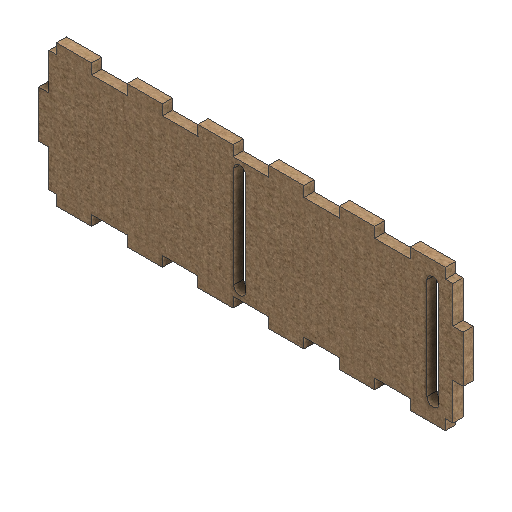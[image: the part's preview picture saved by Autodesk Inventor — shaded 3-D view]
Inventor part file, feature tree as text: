
AUTODESK INVENTOR PART (.ipt)
format: ipt  version: 2025.2 (Build 292293000, 293)  size: 680,448 bytes
history: native  units: mm
features: sketch x7, extrude x4, other x2, mirror x1, projected_geometry x1
ambient origin geometry x8: Origin, YZ Plane, XZ Plane, XY Plane, X Axis, Y Axis, Z Axis, Center Point
bodies: Solid1 (feature_tree)
feature tree (15):
  extrude  "Extrusion1"  Depth=70.0mm
  extrude  "Extrusion2"  Depth=5.1mm
  extrude  "Extrusion4"  Depth=210.0mm
  extrude  "Extrusion3"  Depth=6.0mm
  mirror  "Mirror2"
  sketch  "Sketch5"  dims[d16=53.98mm d17=85.6mm d18=20.0mm d19=0.5mm d20=0.0mm d21=5.0mm d22=40.0mm d24=35.0mm d25=10.0mm d27=10.0mm d29=40.0mm d31=35.0mm d32=10.0mm d34=10.0mm d36=70.0mm d37=23.383333mm]
  sketch  "Sketch1"  dims[d0=210.0mm d1=70.0mm]
  sketch  "Sketch2"  dims[d5=17.6mm d6=210.0mm]
  sketch  "Sketch3"  dims[d13=50.0mm]
  sketch  "Sketch4"  dims[d14=5.0mm d15=0.0mm]
  sketch  "Sketch Rectangular Pattern1"  dims[d3=0.0mm d4=5.1mm]
  sketch  "Sketch Rectangular Pattern2"  dims[d7=5.0mm d8=0.0mm d12=6.0mm]
  projected_geometry  "Projected Loop1"
  other  "Image1"
  other  "Image2"
